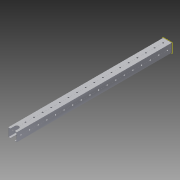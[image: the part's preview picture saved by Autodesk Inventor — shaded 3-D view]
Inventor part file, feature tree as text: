
AUTODESK INVENTOR PART (.ipt)
format: ipt  version: 2014 (Build 180170000, 170)  size: 1,304,576 bytes
history: native  units: in
note: dims shown in document units (in); Inventor stores cm internally (conversion verified against a paired STEP export)
features: extrude x3, sketch x3, pattern_circular x1, other x1, plane x1, imported_body x1
ambient origin geometry x8: Origin, YZ Plane, XZ Plane, XY Plane, X Axis, Y Axis, Z Axis, Center Point
bodies: Body1 (feature_tree)
feature tree (10):
  pattern_circular  "CirPattern2"
  other  "217-3426-STEP1"
  plane  "Work Plane1"
  extrude  "Extrusion1"  Depth=3937.0079in TaperAngle=0.0deg
  extrude  "Extrusion2"  Depth=0.5in TaperAngle=0.0deg
  extrude  "Extrusion4"  [1 undecoded]
  imported_body  "Base1"
  sketch  "Sketch1"  dims[d0=-18.0in d1=3937.0079in d2=0.0in]
  sketch  "Sketch3"  dims[d3=0.5in d4=3.937in d5=0.0in]
  sketch  "Sketch5"  dims[d8=3.937in d9=0.0in]
note: 1 required parameter value undecoded (feature->parameter linkage not recoverable at this tier; creation-order binding heuristic only, values carry confidence <= 0.55)
